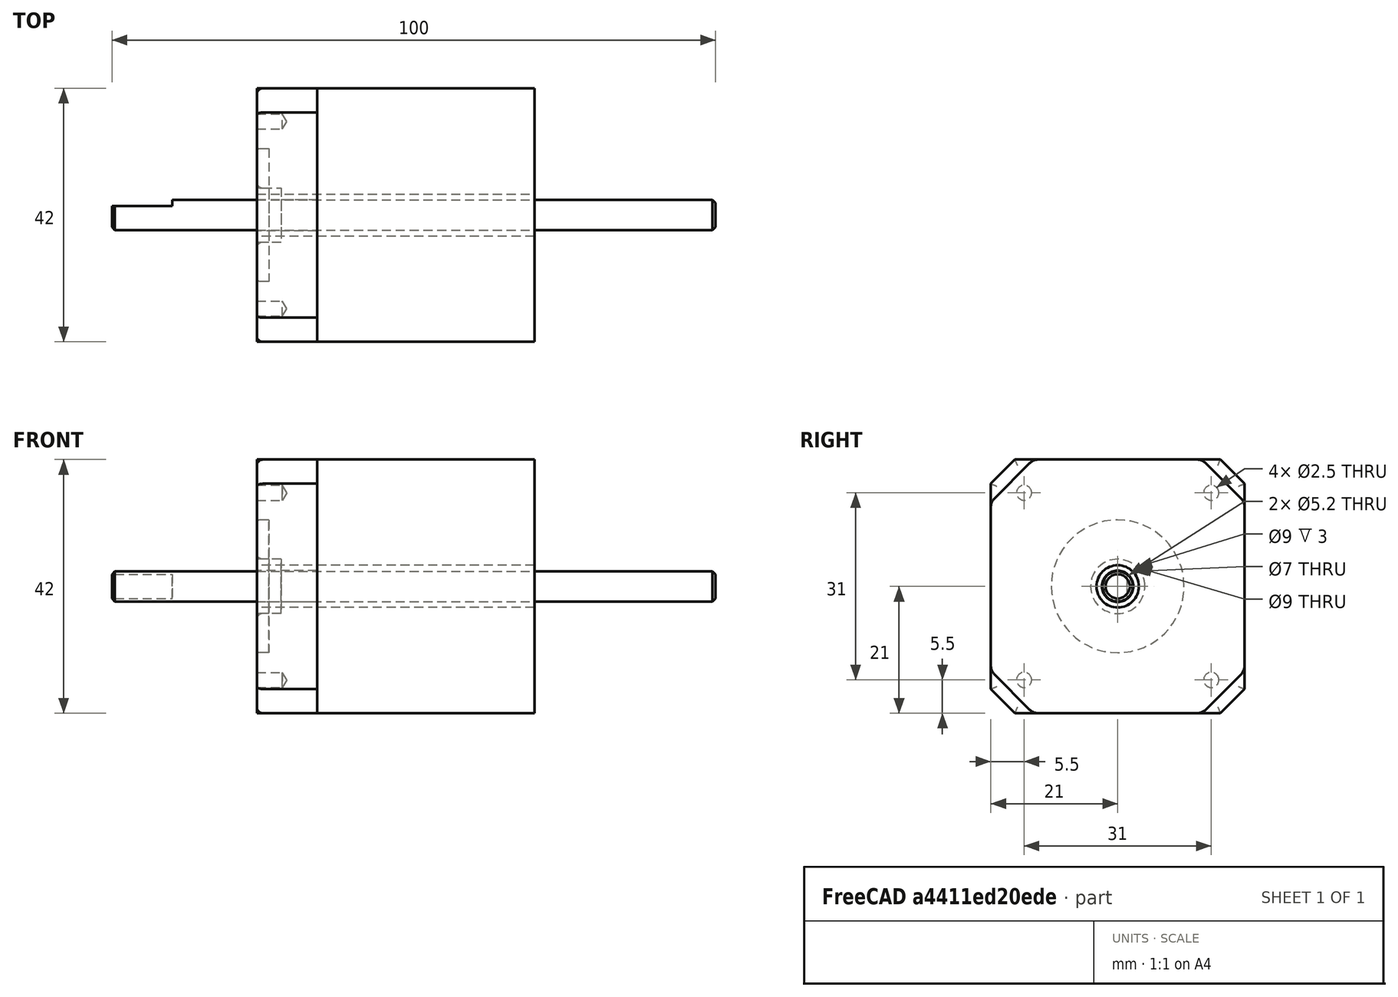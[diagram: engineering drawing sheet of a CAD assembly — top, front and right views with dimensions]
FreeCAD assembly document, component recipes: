
FREECAD ASSEMBLY — COMPONENT RECIPES ("Nema17")

This assembly document has 5 components, labeled P0..P4 below (a component is one placed body or linked part). 5 of them carry a construction recipe — the FreeCAD feature program that regenerates the part from scratch, quoted from this document or its linked companion documents; the rest are supplied as boundary geometry only. No exploded tour is included for this assembly.
COMPONENT P0 — recipe-attached ("EndCap", modeled in this document).
Construction recipe (the document's own serialized feature program — sketch geometry with constraints, then the solid features built on it; lengths are millimeters unless a unit is written):

FEATURE [Sketcher::SketchObject] Sketch007
  MapMode = 5
  Placement = pos=(0,0,0) rot=(0.57735,0.57735,0.57735;2.0944rad)
  Support = -> [YZ_Plane008]
  sketch-geometry (8):
    g0: LineSegment StartX=-21 StartY=17 StartZ=0 EndX=-17 EndY=21 EndZ=0
    g1: LineSegment StartX=-17 StartY=21 StartZ=0 EndX=17 EndY=21 EndZ=0
    g2: LineSegment StartX=17 StartY=21 StartZ=0 EndX=21 EndY=17 EndZ=0
    g3: LineSegment StartX=21 StartY=17 StartZ=0 EndX=21 EndY=-17 EndZ=0
    g4: LineSegment StartX=21 StartY=-17 StartZ=0 EndX=17 EndY=-21 EndZ=0
    g5: LineSegment StartX=17 StartY=-21 StartZ=0 EndX=-17 EndY=-21 EndZ=0
    g6: LineSegment StartX=-17 StartY=-21 StartZ=0 EndX=-21 EndY=-17 EndZ=0
    g7: LineSegment StartX=-21 StartY=-17 StartZ=0 EndX=-21 EndY=17 EndZ=0
  constraints (24):
    c: Coincident(g0,g1)
    c: Horizontal(g1)
    c: Coincident(g1,g2)
    c: Coincident(g2,g3)
    c: Vertical(g3)
    c: Coincident(g3,g4)
    c: Coincident(g4,g5)
    c: Horizontal(g5)
    c: Coincident(g5,g6)
    c: Coincident(g6,g7)
    c: Vertical(g7)
    c: Coincident(g7,g0)
    c: DistanceX(g0,g2) = 42
    c: DistanceY(g5,g0) = 42
    c: Distance(g1) = 34
    c: DistanceY(g0,g0) = 4
    c: Equal(g0,g4)
    c: Equal(g4,g6)
    c: Equal(g6,g2)
    c: Equal(g1,g7)
    c: Equal(g7,g5)
    c: Equal(g5,g3)
    c: DistanceX(g0,g-1) = 21
    c: DistanceY(g-1,g0) = 21
FEATURE [PartDesign::Pad] Pad002
  AllowMultiFace = false
  Direction = (1,1,1)
  Length = 10
  Length2 = 100
  Placement = pos=(0,0,0) rot=(0.57735,0.57735,0.57735;2.0944rad)
  Profile = -> Sketch007
  Type = 0
  expr: Length = Spreadsheet.BackCapLenght
FEATURE [Sketcher::SketchObject] Sketch008
  MapMode = 5
  Placement = pos=(0,0,0) rot=(0.57735,0.57735,-0.57735;4.18879rad)
  Support = -> [Pad002]
  sketch-geometry (1):
    g0: Circle CenterX=0 CenterY=0 CenterZ=0 NormalX=0 NormalY=0 NormalZ=1 AngleXU=0 Radius=4.5
  constraints (2):
    c: Coincident(g-1,g0)
    c: Radius(g0) = 4.5
FEATURE [PartDesign::Pocket] Pocket003
  AllowMultiFace = false
  BaseFeature = -> Pad002
  Length = 4
  Length2 = 100
  Placement = pos=(0,0,0) rot=(0.57735,0.57735,0.57735;2.0944rad)
  Profile = -> Sketch008
  Type = 0
FEATURE [Sketcher::SketchObject] Sketch009
  MapMode = 5
  Placement = pos=(4,-1.8e-15,1.8e-15) rot=(0.57735,0.57735,-0.57735;4.18879rad)
  Support = -> [Pocket003]
  sketch-geometry (1):
    g0: Circle CenterX=0 CenterY=0 CenterZ=0 NormalX=0 NormalY=0 NormalZ=1 AngleXU=0 Radius=2.6
  constraints (2):
    c: Coincident(g0,g-1)
    c: Radius(g0) = 2.6
FEATURE [PartDesign::Pocket] Pocket004
  AllowMultiFace = false
  BaseFeature = -> Pocket003
  Length = 5
  Length2 = 100
  Placement = pos=(0,0,0) rot=(0.57735,0.57735,0.57735;2.0944rad)
  Profile = -> Sketch009
  Type = 1
FEATURE [PartDesign::Fillet] Fillet001
  Base = -> Pocket004 [Face4]
  BaseFeature = -> Pocket004
  Placement = pos=(0,0,0) rot=(0.57735,0.57735,0.57735;2.0944rad)
  Radius = 1
  SupportTransform = true
FEATURE [PartDesign::Body] Body003
  Group = -> [Sketch007,Pad002,Sketch008,Pocket003,Sketch009,Pocket004,Fillet001]
  Origin = -> Origin008
  Tip = -> Fillet001
COMPONENT P1 — recipe-attached ("MiddlePart", modeled in this document).
Construction recipe (the document's own serialized feature program — sketch geometry with constraints, then the solid features built on it; lengths are millimeters unless a unit is written):

FEATURE [Sketcher::SketchObject] Sketch002
  MapMode = 5
  Placement = pos=(0,0,0) rot=(0.57735,0.57735,0.57735;2.0944rad)
  Support = -> [YZ_Plane006]
  sketch-geometry (8):
    g0: LineSegment StartX=-21 StartY=14 StartZ=0 EndX=-14 EndY=21 EndZ=0
    g1: LineSegment StartX=-14 StartY=21 StartZ=0 EndX=14 EndY=21 EndZ=0
    g2: LineSegment StartX=14 StartY=21 StartZ=0 EndX=21 EndY=14 EndZ=0
    g3: LineSegment StartX=21 StartY=14 StartZ=0 EndX=21 EndY=-14 EndZ=0
    g4: LineSegment StartX=21 StartY=-14 StartZ=0 EndX=14 EndY=-21 EndZ=0
    g5: LineSegment StartX=14 StartY=-21 StartZ=0 EndX=-14 EndY=-21 EndZ=0
    g6: LineSegment StartX=-14 StartY=-21 StartZ=0 EndX=-21 EndY=-14 EndZ=0
    g7: LineSegment StartX=-21 StartY=-14 StartZ=0 EndX=-21 EndY=14 EndZ=0
  constraints (24):
    c: Coincident(g0,g1)
    c: Horizontal(g1)
    c: Coincident(g1,g2)
    c: Coincident(g2,g3)
    c: Vertical(g3)
    c: Coincident(g3,g4)
    c: Coincident(g4,g5)
    c: Horizontal(g5)
    c: Coincident(g5,g6)
    c: Coincident(g6,g7)
    c: Vertical(g7)
    c: Coincident(g7,g0)
    c: DistanceX(g0,g2) = 42
    c: DistanceY(g5,g0) = 42
    c: Distance(g1) = 28
    c: Equal(g7,g1)
    c: Equal(g1,g3)
    c: Equal(g3,g5)
    c: DistanceY(g5,g-1) = 21
    c: DistanceX(g0,g-1) = 21
    c: Equal(g6,g2)
    c: Equal(g2,g0)
    c: Equal(g0,g4)
    c: DistanceX(g0,g0) = 7
FEATURE [PartDesign::Pad] Pad
  AllowMultiFace = false
  Direction = (1,1,1)
  Length = 46
  Length2 = 100
  Placement = pos=(0,0,0) rot=(0.57735,0.57735,0.57735;2.0944rad)
  Profile = -> Sketch002
  Type = 0
  expr: Length = Spreadsheet.BodyLength - Spreadsheet.FrontCapLength - Spreadsheet.BackCapLenght
FEATURE [Sketcher::SketchObject] Sketch003
  MapMode = 5
  Placement = pos=(0,0,0) rot=(0.57735,0.57735,-0.57735;4.18879rad)
  Support = -> [Pad]
  sketch-geometry (1):
    g0: Circle CenterX=0 CenterY=0 CenterZ=0 NormalX=0 NormalY=0 NormalZ=1 AngleXU=0 Radius=3.5
  constraints (2):
    c: Coincident(g-1,g0)
    c: Radius(g0) = 3.5
FEATURE [PartDesign::Pocket] Pocket001
  AllowMultiFace = false
  BaseFeature = -> Pad
  Length = 5
  Length2 = 100
  Placement = pos=(0,0,0) rot=(0.57735,0.57735,0.57735;2.0944rad)
  Profile = -> Sketch003
  Type = 1
FEATURE [PartDesign::Fillet] Fillet003
  Base = -> Pocket001 [Edge5,Edge1,Edge2,Edge8,Edge23,Edge25,Edge26,Edge24]
  BaseFeature = -> Pocket001
  Placement = pos=(0,0,0) rot=(0.57735,0.57735,0.57735;2.0944rad)
  Radius = 2
  SupportTransform = true
FEATURE [PartDesign::Body] Body001
  Group = -> [Sketch002,Pad,Sketch003,Pocket001,Fillet003]
  Origin = -> Origin006
  Tip = -> Fillet003
COMPONENT P2 — recipe-attached ("Mutter", modeled in this document).
Construction recipe (the document's own serialized feature program — sketch geometry with constraints, then the solid features built on it; lengths are millimeters unless a unit is written):

FEATURE [Sketcher::SketchObject] Sketch010
  MapMode = 5
  Placement = pos=(0,0,0) rot=(0.57735,0.57735,0.57735;2.0944rad)
  Support = -> [YZ_Plane010]
  expr: Constraints[2] = Spreadsheet.FrontScheibenRaidius
  sketch-geometry (2):
    g0: Circle CenterX=0 CenterY=0 CenterZ=0 NormalX=0 NormalY=0 NormalZ=1 AngleXU=0 Radius=11
    g1: Circle CenterX=0 CenterY=0 CenterZ=0 NormalX=0 NormalY=0 NormalZ=1 AngleXU=0 Radius=4.5
  constraints (4):
    c: Coincident(g0,g-1)
    c: Coincident(g0,g1)
    c: Radius(g0) = 11
    c: Radius(g1) = 4.5
FEATURE [PartDesign::Pad] Pad003
  AllowMultiFace = false
  Direction = (1,1,1)
  Length = 2
  Length2 = 100
  Placement = pos=(0,0,0) rot=(0.57735,0.57735,0.57735;2.0944rad)
  Profile = -> Sketch010
  Type = 0
  expr: Length = Spreadsheet.FrontScheibenThignes
FEATURE [PartDesign::Fillet] Fillet002
  Base = -> Pad003 [Face3]
  BaseFeature = -> Pad003
  Placement = pos=(0,0,0) rot=(0.57735,0.57735,0.57735;2.0944rad)
  Radius = 0.5
  SupportTransform = true
FEATURE [PartDesign::Body] Body004
  Group = -> [Sketch010,Pad003,Fillet002]
  Origin = -> Origin010
  Tip = -> Fillet002
COMPONENT P3 — recipe-attached ("Shaft", modeled in this document).
Construction recipe (the document's own serialized feature program — sketch geometry with constraints, then the solid features built on it; lengths are millimeters unless a unit is written):

FEATURE [Sketcher::SketchObject] Sketch
  MapMode = 5
  Placement = pos=(0,0,0) rot=(1,0,0;1.5708rad)
  Support = -> [XZ_Plane005]
  expr: Constraints[14] = Spreadsheet.FrontShaftLength
  expr: Constraints[15] = Spreadsheet.BodyLength + Spreadsheet.BackShaftLength
  sketch-geometry (6):
    g0: LineSegment StartX=-24 StartY=0 StartZ=0 EndX=-24 EndY=2 EndZ=0
    g1: LineSegment StartX=-24 StartY=2 StartZ=0 EndX=-23.5 EndY=2.5 EndZ=0
    g2: LineSegment StartX=-23.5 StartY=2.5 StartZ=0 EndX=75.5 EndY=2.5 EndZ=0
    g3: LineSegment StartX=75.5 StartY=2.5 StartZ=0 EndX=76 EndY=2 EndZ=0
    g4: LineSegment StartX=76 StartY=2 StartZ=0 EndX=76 EndY=0 EndZ=0
    g5: LineSegment StartX=76 StartY=0 StartZ=0 EndX=-24 EndY=0 EndZ=0
  constraints (18):
    c: Vertical(g0)
    c: Coincident(g0,g1)
    c: Coincident(g1,g2)
    c: Horizontal(g2)
    c: Coincident(g2,g3)
    c: Coincident(g3,g4)
    c: Vertical(g4)
    c: Coincident(g4,g5)
    c: Horizontal(g5)
    c: Coincident(g0,g5)
    c: PointOnObject(g0,g-1)
    c: DistanceY(g-1,g1) = 2.5
    c: DistanceX(g0,g1) = 0.5
    c: DistanceX(g2,g3) = 0.5
    c: DistanceX(g0,g-1) = 24
    c: DistanceX(g-1,g4) = 76
    c: DistanceY(g0,g1) = 0.5
    c: DistanceY(g3,g2) = 0.5
FEATURE [PartDesign::Revolution] Revolution
  AllowMultiFace = false
  Angle = 360
  Axis = (1,0,0)
  Base = (0,0,0)
  Placement = pos=(0,0,0) rot=(1,0,0;1.5708rad)
  Profile = -> Sketch
  ReferenceAxis = -> X_Axis005
  Reversed = true
FEATURE [Sketcher::SketchObject] Sketch001
  MapMode = 5
  Placement = pos=(-24,0,0) rot=(0.707107,0,-0.707107;3.14159rad)
  Support = -> [Revolution]
  expr: Constraints[11] = Spreadsheet.ShaftCutinDeth
  sketch-geometry (4):
    g0: LineSegment StartX=-2.5 StartY=-1.5 StartZ=0 EndX=2.5 EndY=-1.5 EndZ=0
    g1: LineSegment StartX=2.5 StartY=-1.5 StartZ=0 EndX=2.5 EndY=-2.5 EndZ=0
    g2: LineSegment StartX=2.5 StartY=-2.5 StartZ=0 EndX=-2.5 EndY=-2.5 EndZ=0
    g3: LineSegment StartX=-2.5 StartY=-2.5 StartZ=0 EndX=-2.5 EndY=-1.5 EndZ=0
  constraints (12):
    c: Coincident(g0,g1)
    c: Coincident(g1,g2)
    c: Coincident(g2,g3)
    c: Coincident(g3,g0)
    c: Horizontal(g0)
    c: Horizontal(g2)
    c: Vertical(g1)
    c: Vertical(g3)
    c: Distance(g0) = 5
    c: DistanceX(g0,g-1) = 2.5
    c: DistanceY(g2,g-1) = 2.5
    c: DistanceY(g1,g1) = 1
FEATURE [PartDesign::Pocket] Pocket
  AllowMultiFace = false
  BaseFeature = -> Revolution
  Length = 10
  Length2 = 100
  Placement = pos=(0,0,0) rot=(1,0,0;1.5708rad)
  Profile = -> Sketch001
  Type = 0
  expr: Length = Spreadsheet.ShaftCutinLength
FEATURE [PartDesign::Body] Body
  Group = -> [Sketch,Revolution,Sketch001,Pocket]
  Origin = -> Origin005
  Tip = -> Pocket
COMPONENT P4 — recipe-attached ("TopCap", modeled in this document).
Construction recipe (the document's own serialized feature program — sketch geometry with constraints, then the solid features built on it; lengths are millimeters unless a unit is written):

FEATURE [Sketcher::SketchObject] Sketch004
  MapMode = 5
  Placement = pos=(0,0,0) rot=(0.57735,0.57735,0.57735;2.0944rad)
  Support = -> [YZ_Plane007]
  sketch-geometry (8):
    g0: LineSegment StartX=-21 StartY=17 StartZ=0 EndX=-21 EndY=-17 EndZ=0
    g1: LineSegment StartX=-21 StartY=-17 StartZ=0 EndX=-17 EndY=-21 EndZ=0
    g2: LineSegment StartX=-17 StartY=-21 StartZ=0 EndX=17 EndY=-21 EndZ=0
    g3: LineSegment StartX=17 StartY=-21 StartZ=0 EndX=21 EndY=-17 EndZ=0
    g4: LineSegment StartX=21 StartY=-17 StartZ=0 EndX=21 EndY=17 EndZ=0
    g5: LineSegment StartX=21 StartY=17 StartZ=0 EndX=17 EndY=21 EndZ=0
    g6: LineSegment StartX=17 StartY=21 StartZ=0 EndX=-17 EndY=21 EndZ=0
    g7: LineSegment StartX=-17 StartY=21 StartZ=0 EndX=-21 EndY=17 EndZ=0
  constraints (24):
    c: Vertical(g0)
    c: Coincident(g0,g1)
    c: Coincident(g1,g2)
    c: Horizontal(g2)
    c: Coincident(g2,g3)
    c: Coincident(g3,g4)
    c: Vertical(g4)
    c: Coincident(g4,g5)
    c: Coincident(g5,g6)
    c: Horizontal(g6)
    c: Coincident(g6,g7)
    c: Coincident(g0,g7)
    c: DistanceX(g0,g4) = 42
    c: DistanceY(g1,g6) = 42
    c: DistanceX(g0,g-1) = 21
    c: DistanceY(g1,g-1) = 21
    c: DistanceX(g6,g6) = 34
    c: Equal(g6,g0)
    c: Equal(g0,g2)
    c: Equal(g2,g4)
    c: DistanceX(g0,g6) = 4
    c: Equal(g7,g5)
    c: Equal(g5,g1)
    c: Equal(g1,g3)
FEATURE [PartDesign::Pad] Pad001
  AllowMultiFace = false
  Direction = (1,1,1)
  Length = 10
  Length2 = 100
  Placement = pos=(0,0,0) rot=(0.57735,0.57735,0.57735;2.0944rad)
  Profile = -> Sketch004
  Type = 0
  expr: Length = Spreadsheet.FrontCapLength
FEATURE [Sketcher::SketchObject] Sketch005
  MapMode = 5
  Placement = pos=(0,0,0) rot=(0.57735,0.57735,-0.57735;4.18879rad)
  Support = -> [Pad001]
  sketch-geometry (1):
    g0: Circle CenterX=0 CenterY=0 CenterZ=0 NormalX=0 NormalY=0 NormalZ=1 AngleXU=0 Radius=2.6
  constraints (2):
    c: Coincident(g0,g-1)
    c: Radius(g0) = 2.6
FEATURE [PartDesign::Pocket] Pocket002
  AllowMultiFace = false
  BaseFeature = -> Pad001
  Length = 5
  Length2 = 100
  Placement = pos=(0,0,0) rot=(0.57735,0.57735,0.57735;2.0944rad)
  Profile = -> Sketch005
  Type = 1
FEATURE [Sketcher::SketchObject] Sketch006
  MapMode = 5
  Placement = pos=(0,0,0) rot=(0.57735,0.57735,-0.57735;4.18879rad)
  Support = -> [Pocket002]
  sketch-geometry (8):
    g0: LineSegment [constr] StartX=-15.5 StartY=15.5 StartZ=0 EndX=15.5 EndY=15.5 EndZ=0
    g1: LineSegment [constr] StartX=15.5 StartY=15.5 StartZ=0 EndX=15.5 EndY=-15.5 EndZ=0
    g2: LineSegment [constr] StartX=15.5 StartY=-15.5 StartZ=0 EndX=-15.5 EndY=-15.5 EndZ=0
    g3: LineSegment [constr] StartX=-15.5 StartY=-15.5 StartZ=0 EndX=-15.5 EndY=15.5 EndZ=0
    g4: Circle CenterX=-15.5 CenterY=15.5 CenterZ=0 NormalX=0 NormalY=0 NormalZ=1 AngleXU=0 Radius=1.5
    g5: Circle CenterX=15.5 CenterY=15.5 CenterZ=0 NormalX=0 NormalY=0 NormalZ=1 AngleXU=0 Radius=1.5
    g6: Circle CenterX=15.5 CenterY=-15.5 CenterZ=0 NormalX=0 NormalY=0 NormalZ=1 AngleXU=0 Radius=1.5
    g7: Circle CenterX=-15.5 CenterY=-15.5 CenterZ=0 NormalX=0 NormalY=0 NormalZ=1 AngleXU=0 Radius=1.5
  constraints (20):
    c: Coincident(g0,g1)
    c: Coincident(g1,g2)
    c: Coincident(g2,g3)
    c: Coincident(g3,g0)
    c: Horizontal(g0)
    c: Horizontal(g2)
    c: Vertical(g1)
    c: Vertical(g3)
    c: Equal(g3,g0)
    c: Distance(g0) = 31
    c: DistanceX(g0,g-1) = 15.5
    c: DistanceY(g2,g-1) = 15.5
    c: Radius(g4) = 1.5
    c: Equal(g4,g5) = 1.5
    c: Equal(g6,g5)
    c: Equal(g7,g6)
    c: Coincident(g7,g2)
    c: Coincident(g4,g0)
    c: Coincident(g5,g0)
    c: Coincident(g6,g1)
FEATURE [PartDesign::Hole] Hole
  AllowMultiFace = false
  BaseFeature = -> Pocket002
  Depth = 5
  DepthType = 0
  Diameter = 1.1
  DrillPoint = 1
  DrillPointAngle = 118
  HoleCutCountersinkAngle = 90
  HoleCutDepth = 0
  HoleCutDiameter = 3
  HoleCutType = 0
  ModelActualThread = false
  Placement = pos=(0,0,0) rot=(0.57735,0.57735,0.57735;2.0944rad)
  Profile = -> Sketch006
  Tapered = false
  TaperedAngle = 90
  ThreadAngle = 60
  ThreadClass = 0
  ThreadCutOffInner = 0.032476
  ThreadCutOffOuter = 0.0649519
  ThreadDirection = 0
  ThreadFit = 0
  ThreadPitch = 0.3
  ThreadSize = 3
  ThreadType = 1
  Threaded = true
FEATURE [PartDesign::Fillet] Fillet
  Base = -> Hole [Edge11,Edge6,Edge3,Edge9,Edge12,Edge14,Edge15,Edge13]
  BaseFeature = -> Hole
  Placement = pos=(0,0,0) rot=(0.57735,0.57735,0.57735;2.0944rad)
  Radius = 1
  SupportTransform = true
FEATURE [PartDesign::Body] Body002
  Group = -> [Sketch004,Pad001,Sketch005,Pocket002,Sketch006,Hole,Fillet]
  Origin = -> Origin007
  Tip = -> Fillet
PROVENANCE & LICENSES
A FreeCAD (.FCStd) document from a public repository crawl; recipes are the document's own serialized feature recipes (and, for linked parts, companion documents' recipes).
License: as declared in the source repository (recorded in the dataset sidecar).
